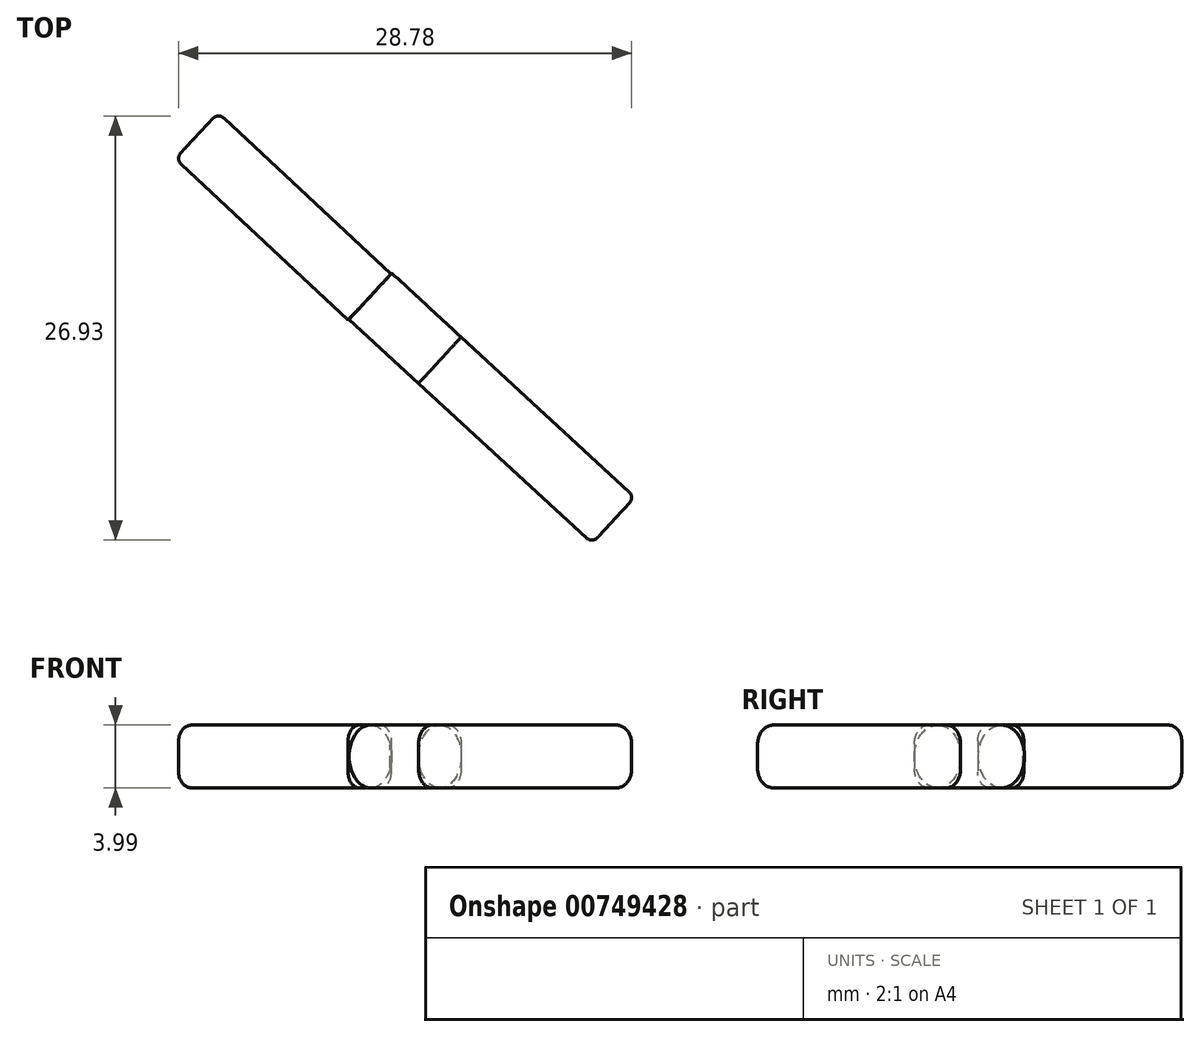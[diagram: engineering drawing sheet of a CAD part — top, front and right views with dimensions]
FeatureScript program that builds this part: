
annotation { "Feature Type Name" : "Feature", "Feature Type Description" : "" }
export const myFeature = defineFeature(function(context is Context, id is Id, definition is map)
    precondition{}
    {
        {
            var Q0;
            Q0=qCreatedBy(makeId("Top.planeOp"),FACE);
            var sketch = newSketch(context, id + "F0", { "sketchPlane" : qUnion([Q0])});
            skLineSegment(sketch, "E0", {"start": v(0, 0) * mm, "end": v(11.03, -10.16) * mm});
            skLineSegment(sketch, "E1", {"start": v(11.03, -10.16) * mm, "end": v(8.33, -13.1) * mm});
            skLineSegment(sketch, "E2", {"start": v(8.33, -13.1) * mm, "end": v(-2.7, -2.93) * mm});
            skLineSegment(sketch, "E3", {"start": v(-2.7, -2.93) * mm, "end": v(0, 0) * mm});
            skLineSegment(sketch, "E4", {"start": v(-4.46, 4) * mm, "end": v(-15.43, 14.25) * mm});
            skLineSegment(sketch, "E5", {"start": v(-15.43, 14.25) * mm, "end": v(-18.15, 11.33) * mm});
            skLineSegment(sketch, "E6", {"start": v(-18.15, 11.33) * mm, "end": v(-7.18, 1.1) * mm});
            skLineSegment(sketch, "E7", {"start": v(-7.18, 1.1) * mm, "end": v(-4.46, 4) * mm});
            skSolve(sketch);
        }
        {
            var Q0;
            Q0 = qSketchRegion(id + "F0", true);
            extrude(context, id + "F1", {"entities" : qUnion([Q0]), "depth" : 4 * mm, "offsetDistance" : 25.4 * mm});
        }
        {
            var Q0;
            Q0=makeQuery(id+"F1.opExtrude","SWEPT_FACE",FACE,{"disambiguationData":[OSD([sQuery(id+"F0.wireOp",EDGE,"E3")])]});
            var sketch = newSketch(context, id + "F2", { "sketchPlane" : qUnion([Q0])});
            skLineSegment(sketch, "E8", {"start": v(2, 3.99) * mm, "end": v(2, 0) * mm});
            skLineSegment(sketch, "E9", {"start": v(2, 0) * mm, "end": v(0, 2) * mm});
            skLineSegment(sketch, "E10", {"start": v(0, 2) * mm, "end": v(3.99, 2) * mm});
            skLineSegment(sketch, "E11", {"start": v(3.99, 2) * mm, "end": v(2, 3.99) * mm});
            skCircle(sketch, "E12", {"center": v(2, 2) * mm, "radius": 2 * mm});
            skSolve(sketch);
        }
        {
            var Q0;
            Q0 = qSketchRegion(id + "F2", true);
            extrude(context, id + "F3", {"entities" : qUnion([Q0]), "operationType" : NewBodyOperationType.ADD, "depth" : 6 * mm, "offsetDistance" : 25.4 * mm});
        }
        {
            var Q0;
            Q0=makeQuery(id+"F1.opExtrude","CAP_EDGE",EDGE,{"disambiguationData":[OSD([sQuery(id+"F0.wireOp",EDGE,"E0")])],"isStart":false});
            var Q1;
            Q1=makeQuery(id+"F1.opExtrude","CAP_EDGE",EDGE,{"disambiguationData":[OSD([sQuery(id+"F0.wireOp",EDGE,"E0")])],"isStart":true});
            var Q2;
            Q2=makeQuery(id+"F1.opExtrude","CAP_EDGE",EDGE,{"disambiguationData":[OSD([sQuery(id+"F0.wireOp",EDGE,"E2")])],"isStart":false});
            var Q3;
            Q3=makeQuery(id+"F1.opExtrude","CAP_EDGE",EDGE,{"disambiguationData":[OSD([sQuery(id+"F0.wireOp",EDGE,"E2")])],"isStart":true});
            fillet(context, id + "F4", {"entities" : qUnion([Q0, Q1, Q2, Q3]), "radius" : 1.2 * mm, "tangentPropagation" : true, "allowEdgeOverflow" : false});
        }
        {
            var Q0;
            Q0=makeQuery(id+"F1.opExtrude","CAP_EDGE",EDGE,{"disambiguationData":[OSD([sQuery(id+"F0.wireOp",EDGE,"E6")])],"isStart":false});
            var Q1;
            Q1=makeQuery(id+"F1.opExtrude","CAP_EDGE",EDGE,{"disambiguationData":[OSD([sQuery(id+"F0.wireOp",EDGE,"E6")])],"isStart":true});
            var Q2;
            Q2=makeQuery(id+"F1.opExtrude","CAP_EDGE",EDGE,{"disambiguationData":[OSD([sQuery(id+"F0.wireOp",EDGE,"E4")])],"isStart":true});
            var Q3;
            Q3=makeQuery(id+"F1.opExtrude","CAP_EDGE",EDGE,{"disambiguationData":[OSD([sQuery(id+"F0.wireOp",EDGE,"E4")])],"isStart":false});
            fillet(context, id + "F5", {"entities" : qUnion([Q0, Q1, Q2, Q3]), "radius" : 1 * mm, "tangentPropagation" : true, "allowEdgeOverflow" : false});
        }
        {
            var Q0;
            Q0=makeQuery(id+"F1.opExtrude","SWEPT_FACE",FACE,{"disambiguationData":[OSD([sQuery(id+"F0.wireOp",EDGE,"E1")])]});
            var Q1;
            Q1=makeQuery(id+"F1.opExtrude","SWEPT_FACE",FACE,{"disambiguationData":[OSD([sQuery(id+"F0.wireOp",EDGE,"E5")])]});
            fillet(context, id + "F6", {"entities" : qUnion([Q0, Q1]), "radius" : 0.5 * mm, "tangentPropagation" : true, "allowEdgeOverflow" : false});
        }
    });
